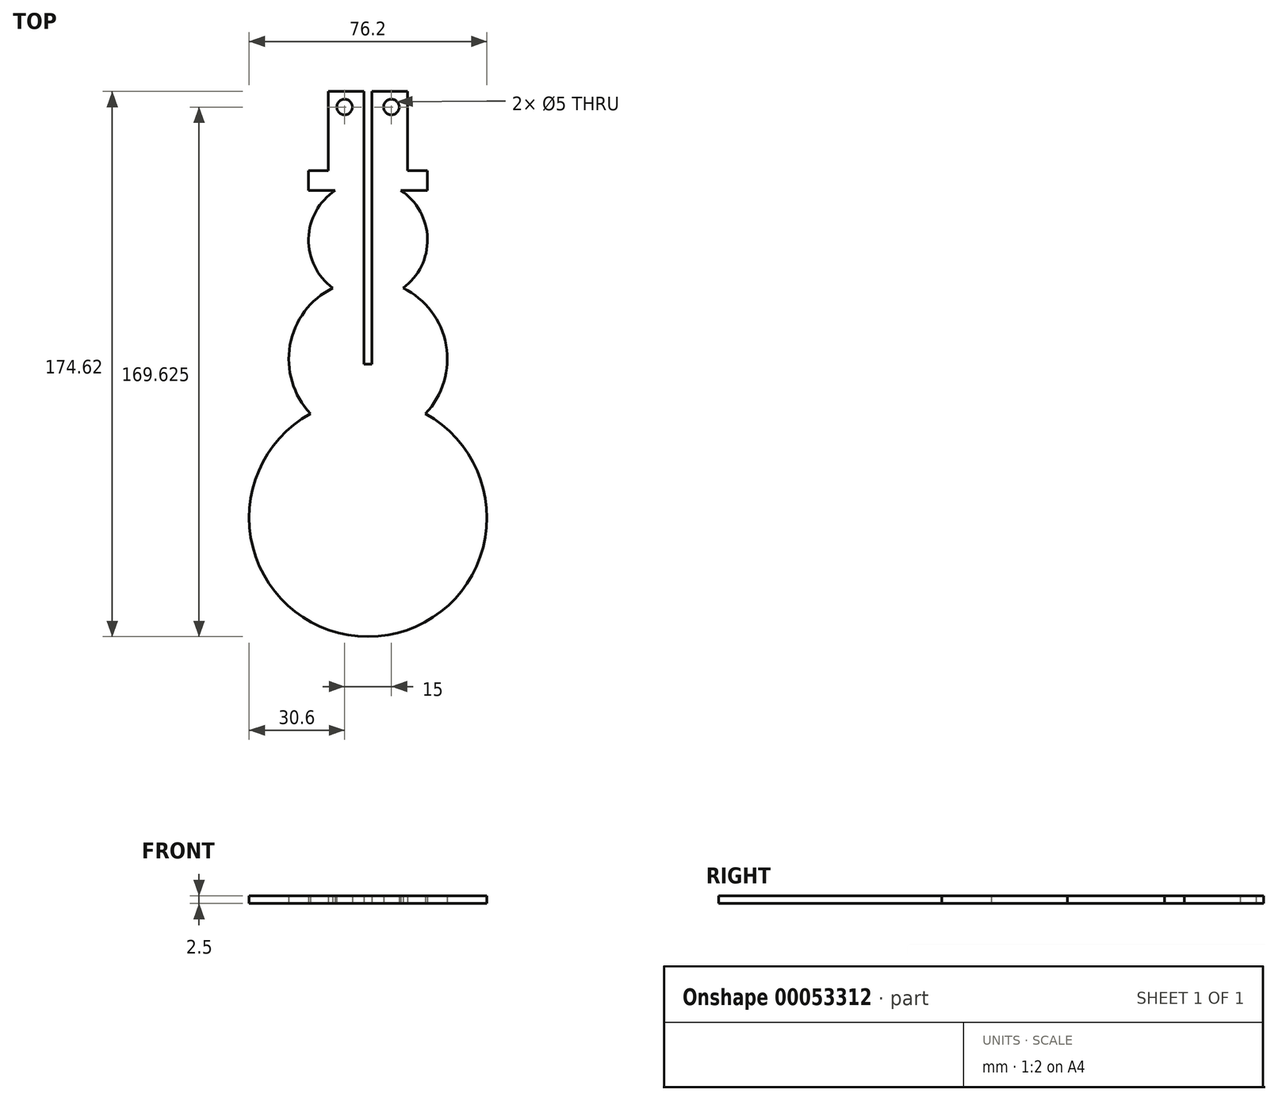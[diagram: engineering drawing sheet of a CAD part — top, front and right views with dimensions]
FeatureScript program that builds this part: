
annotation { "Feature Type Name" : "Feature", "Feature Type Description" : "" }
export const myFeature = defineFeature(function(context is Context, id is Id, definition is map)
    precondition{}
    {
        {
            var Q0;
            Q0=qCreatedBy(makeId("Top.planeOp"),FACE);
            var sketch = newSketch(context, id + "F0", { "sketchPlane" : qUnion([Q0])});
            skCircle(sketch, "E0", {"center": v(0, 38.1) * mm, "radius": 19.05 * mm});
            skCircle(sketch, "E1", {"center": v(0, 0) * mm, "radius": 25.4 * mm});
            skCircle(sketch, "E2", {"center": v(0, -50.8) * mm, "radius": 38.1 * mm});
            skLineSegment(sketch, "E3.bottom", {"start": v(-19.05, 60.33) * mm, "end": v(19.05, 60.33) * mm});
            skLineSegment(sketch, "E3.top", {"start": v(-19.05, 53.98) * mm, "end": v(19.05, 53.98) * mm});
            skLineSegment(sketch, "E3.left", {"start": v(-19.05, 60.33) * mm, "end": v(-19.05, 53.97) * mm});
            skLineSegment(sketch, "E3.right", {"start": v(19.05, 60.33) * mm, "end": v(19.05, 53.97) * mm});
            skLineSegment(sketch, "E4.bottom", {"start": v(-12.7, 60.33) * mm, "end": v(12.7, 60.33) * mm});
            skLineSegment(sketch, "E4.top", {"start": v(-12.7, 85.72) * mm, "end": v(12.7, 85.72) * mm});
            skLineSegment(sketch, "E4.left", {"start": v(-12.7, 60.33) * mm, "end": v(-12.7, 85.72) * mm});
            skLineSegment(sketch, "E4.right", {"start": v(12.7, 60.33) * mm, "end": v(12.7, 85.72) * mm});
            skLineSegment(sketch, "E5.rect.bottom", {"start": v(1.25, 85.72) * mm, "end": v(-1.25, 85.72) * mm});
            skLineSegment(sketch, "E5.rect.top", {"start": v(1.25, -1.59) * mm, "end": v(-1.25, -1.59) * mm});
            skLineSegment(sketch, "E5.rect.left", {"start": v(1.25, 85.72) * mm, "end": v(1.25, -1.59) * mm});
            skLineSegment(sketch, "E5.rect.right", {"start": v(-1.25, 85.72) * mm, "end": v(-1.25, -1.59) * mm});
            skPoint(sketch, "E5.rect.middle", {"position": v(0, 42.07) * mm});
            skCircle(sketch, "E6", {"center": v(-7.5, 80.72) * mm, "radius": 2.5 * mm});
            skCircle(sketch, "E7.MirrorC", {"center": v(7.5, 80.72) * mm, "radius": 2.5 * mm});
            skSolve(sketch);
        }
        {
            var Q0;
            {var subQ0=sQuery(id+"F0.wireOp",EDGE,"E4.right");Q0=makeQuery(id+"F0.imprint","IMPRINT",FACE,{"disambiguationData":[TD([[makeQuery(id+"F0.imprint","IMPRINT",EDGE,{"derivedFrom":subQ0}),1.0]])]});}
            var Q1;
            {var subQ0=sQuery(id+"F0.wireOp",EDGE,"E4.left");Q1=makeQuery(id+"F0.imprint","IMPRINT",FACE,{"disambiguationData":[TD([[makeQuery(id+"F0.imprint","IMPRINT",EDGE,{"derivedFrom":subQ0}),-1.0]])]});}
            var Q2;
            {var subQ0=sQuery(id+"F0.wireOp",EDGE,"E3.left");Q2=makeQuery(id+"F0.imprint","IMPRINT",FACE,{"disambiguationData":[TD([[makeQuery(id+"F0.imprint","IMPRINT",EDGE,{"derivedFrom":subQ0}),1.0]])]});}
            var Q3;
            {var subQ0=sQuery(id+"F0.wireOp",EDGE,"E3.right");Q3=makeQuery(id+"F0.imprint","IMPRINT",FACE,{"disambiguationData":[TD([[makeQuery(id+"F0.imprint","IMPRINT",EDGE,{"derivedFrom":subQ0}),-1.0]])]});}
            var Q4;
            {var subQ0=sQuery(id+"F0.wireOp",EDGE,"E3.top");var subQ1=sQuery(id+"F0.wireOp",EDGE,"E0");var subQ2=makeQuery(id+"F0.imprint","INTERSECT",VERTEX,{"disambiguationData":[OD(0.0)],"derivedFrom":[subQ1,subQ0]});Q4=makeQuery(id+"F0.imprint","IMPRINT",FACE,{"disambiguationData":[TD([[makeQuery(id+"F0.imprint","IMPRINT",EDGE,{"disambiguationData":[TD([[subQ2,-1.0]])],"derivedFrom":subQ1}),1.0]])]});}
            var Q5;
            {var subQ0=sQuery(id+"F0.wireOp",EDGE,"E3.top");var subQ1=sQuery(id+"F0.wireOp",EDGE,"E0");var subQ2=makeQuery(id+"F0.imprint","INTERSECT",VERTEX,{"disambiguationData":[OD(1.0)],"derivedFrom":[subQ1,subQ0]});Q5=makeQuery(id+"F0.imprint","IMPRINT",FACE,{"disambiguationData":[TD([[makeQuery(id+"F0.imprint","IMPRINT",EDGE,{"disambiguationData":[TD([[subQ2,1.0]])],"derivedFrom":subQ1}),1.0]])]});}
            var Q6;
            {var subQ0=sQuery(id+"F0.wireOp",EDGE,"E3.top");var subQ1=sQuery(id+"F0.wireOp",EDGE,"E0");var subQ2=makeQuery(id+"F0.imprint","INTERSECT",VERTEX,{"disambiguationData":[OD(1.0)],"derivedFrom":[subQ1,subQ0]});Q6=makeQuery(id+"F0.imprint","IMPRINT",FACE,{"disambiguationData":[TD([[makeQuery(id+"F0.imprint","IMPRINT",EDGE,{"disambiguationData":[TD([[subQ2,-1.0]])],"derivedFrom":subQ1}),1.0]])]});}
            var Q7;
            {var subQ0=sQuery(id+"F0.wireOp",EDGE,"E3.top");var subQ1=sQuery(id+"F0.wireOp",EDGE,"E0");var subQ2=makeQuery(id+"F0.imprint","INTERSECT",VERTEX,{"disambiguationData":[OD(0.0)],"derivedFrom":[subQ1,subQ0]});Q7=makeQuery(id+"F0.imprint","IMPRINT",FACE,{"disambiguationData":[TD([[makeQuery(id+"F0.imprint","IMPRINT",EDGE,{"disambiguationData":[TD([[subQ2,1.0]])],"derivedFrom":subQ1}),1.0]])]});}
            var Q8;
            {var subQ11=sQuery(id+"F0.wireOp",EDGE,"d17c0fab-f452-4c54-aca8-dd72fcf6b8fe.top");Q8=makeQuery(id+"F0.imprint","IMPRINT",FACE,{"disambiguationData":[TD([[makeQuery(id+"F0.imprint","IMPRINT",EDGE,{"derivedFrom":subQ11}),-1.0]])]});}
            var Q9;
            {var subQ0=sQuery(id+"F0.wireOp",EDGE,"E1");var subQ1=sQuery(id+"F0.wireOp",EDGE,"E0");var subQ2=makeQuery(id+"F0.imprint","INTERSECT",VERTEX,{"disambiguationData":[OD(0.0)],"derivedFrom":[subQ1,subQ0]});Q9=makeQuery(id+"F0.imprint","IMPRINT",FACE,{"disambiguationData":[TD([[makeQuery(id+"F0.imprint","IMPRINT",EDGE,{"disambiguationData":[TD([[subQ2,-1.0]])],"derivedFrom":subQ1}),1.0]])]});}
            var Q10;
            {var subQ0=sQuery(id+"F0.wireOp",EDGE,"E1");var subQ1=sQuery(id+"F0.wireOp",EDGE,"E0");var subQ2=makeQuery(id+"F0.imprint","INTERSECT",VERTEX,{"disambiguationData":[OD(1.0)],"derivedFrom":[subQ1,subQ0]});Q10=makeQuery(id+"F0.imprint","IMPRINT",FACE,{"disambiguationData":[TD([[makeQuery(id+"F0.imprint","IMPRINT",EDGE,{"disambiguationData":[TD([[subQ2,1.0]])],"derivedFrom":subQ1}),1.0]])]});}
            var Q11;
            {var subQ0=sQuery(id+"F0.wireOp",EDGE,"E2");var subQ1=sQuery(id+"F0.wireOp",EDGE,"E1");var subQ2=makeQuery(id+"F0.imprint","INTERSECT",VERTEX,{"disambiguationData":[OD(0.0)],"derivedFrom":[subQ1,subQ0]});Q11=makeQuery(id+"F0.imprint","IMPRINT",FACE,{"disambiguationData":[TD([[makeQuery(id+"F0.imprint","IMPRINT",EDGE,{"disambiguationData":[TD([[subQ2,-1.0]])],"derivedFrom":subQ1}),1.0]])]});}
            var Q12;
            {var subQ0=sQuery(id+"F0.wireOp",EDGE,"E2");var subQ1=sQuery(id+"F0.wireOp",EDGE,"E1");var subQ2=makeQuery(id+"F0.imprint","INTERSECT",VERTEX,{"disambiguationData":[OD(0.0)],"derivedFrom":[subQ1,subQ0]});Q12=makeQuery(id+"F0.imprint","IMPRINT",FACE,{"disambiguationData":[TD([[makeQuery(id+"F0.imprint","IMPRINT",EDGE,{"disambiguationData":[TD([[subQ2,-1.0]])],"derivedFrom":subQ1}),-1.0]])]});}
            var Q13;
            {var subQ11=sQuery(id+"F0.wireOp",EDGE,"E5.rect.top");Q13=makeQuery(id+"F0.imprint","IMPRINT",FACE,{"disambiguationData":[TD([[makeQuery(id+"F0.imprint","IMPRINT",EDGE,{"derivedFrom":subQ11}),1.0]])]});}
            extrude(context, id + "F1", {"entities" : qUnion([Q0, Q1, Q2, Q3, Q4, Q5, Q6, Q7, Q8, Q9, Q10, Q11, Q12, Q13]), "depth" : 2.5 * mm});
        }
    });
